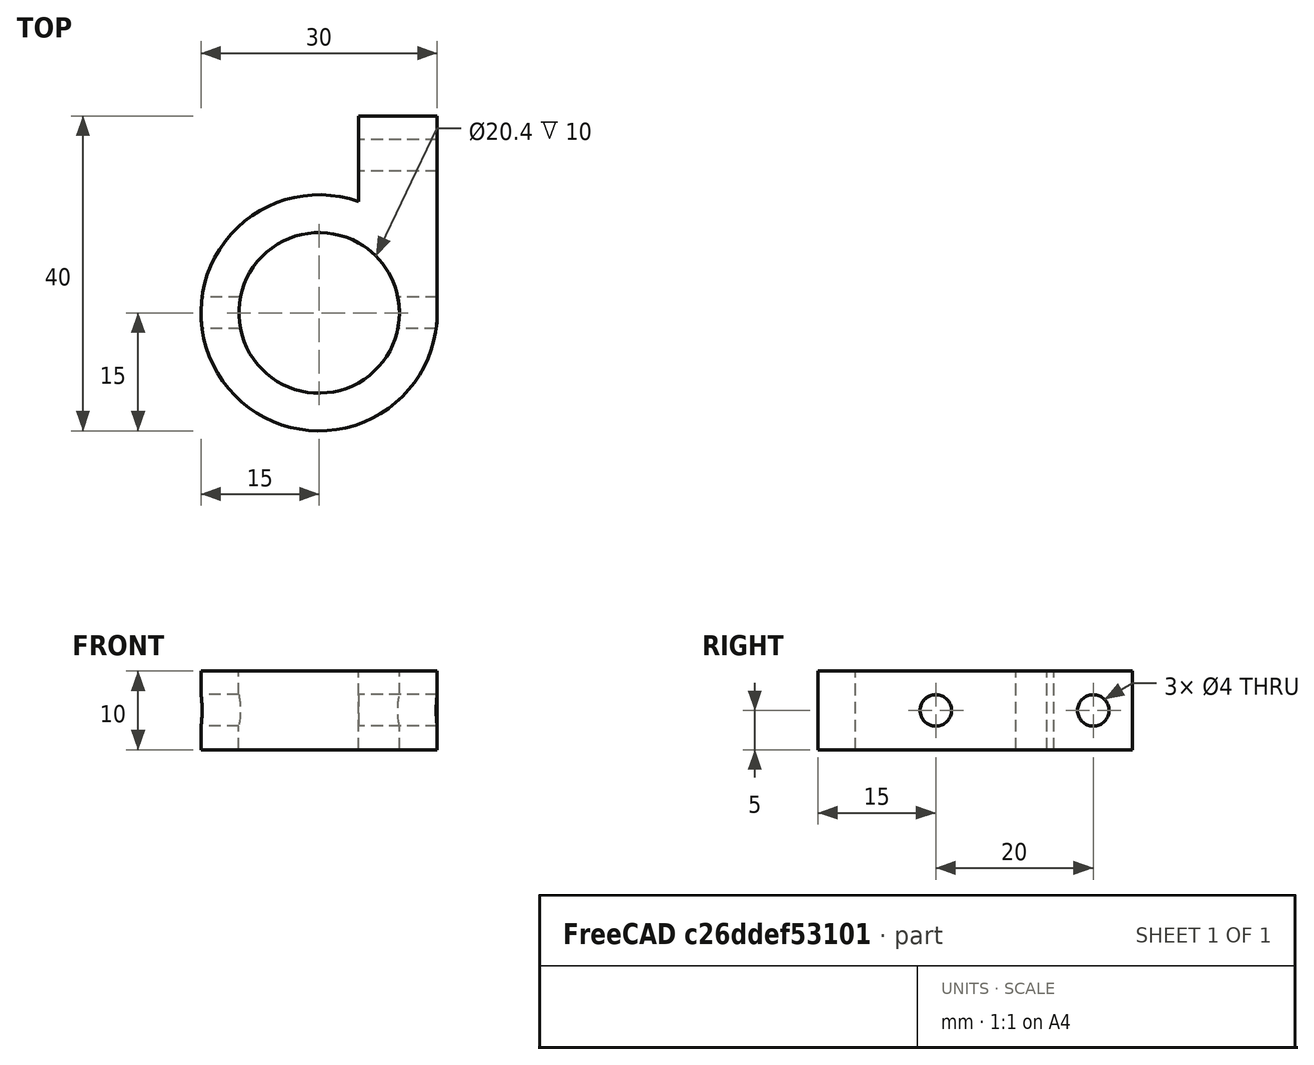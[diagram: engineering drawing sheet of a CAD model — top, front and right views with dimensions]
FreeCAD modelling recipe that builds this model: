
FCSTD DOCUMENT  (FreeCAD 0.18R16110 (Git))
Label: BaseAttachmentSide
License: All rights reserved
LicenseURL: http://en.wikipedia.org/wiki/All_rights_reserved
objects: Part::Cylinder×4, Part::MultiFuse×2, Part::Box×1, Part::Cut×1
note: 8 computed .brp shape members not serialized (recipe doc carries the construction recipe); baked Part::Feature solids carry a one-line shape summary decoded from their .brp

FEATURE [Part::Cylinder] Cylinder
  Angle = 360
  AttacherType = Attacher::AttachEngine3D
  Height = 10
  Placement = pos=(0,0,-5) rot=(0,0,1;0rad)
  Radius = 15
FEATURE [Part::Cylinder] Cylinder001
  Angle = 360
  AttacherType = Attacher::AttachEngine3D
  Height = 10
  Placement = pos=(0,0,-5) rot=(0,0,1;0rad)
  Radius = 10.2
FEATURE [Part::Box] Box  label="Cube"
  AttacherType = Attacher::AttachEngine3D
  Height = 10
  Length = 10
  Placement = pos=(5,0,-5) rot=(0,0,1;0rad)
  Width = 25
FEATURE [Part::Cylinder] Cylinder003
  Angle = 360
  AttacherType = Attacher::AttachEngine3D
  Height = 10
  Placement = pos=(15,20,-1e-16) rot=(0,-1,0;1.5708rad)
  Radius = 2
FEATURE [Part::MultiFuse] Fusion001  label="Positive Fusion"
  Shapes = -> [Cylinder,Box]
FEATURE [Part::Cylinder] Cylinder004
  Angle = 360
  AttacherType = Attacher::AttachEngine3D
  Height = 30
  Placement = pos=(15,0,0) rot=(0,-1,0;1.5708rad)
  Radius = 2
FEATURE [Part::MultiFuse] Fusion  label="Negative Fusion"
  Shapes = -> [Cylinder001,Cylinder003,Cylinder004]
FEATURE [Part::Cut] Cut
  Base = -> Fusion001
  Tool = -> Fusion
